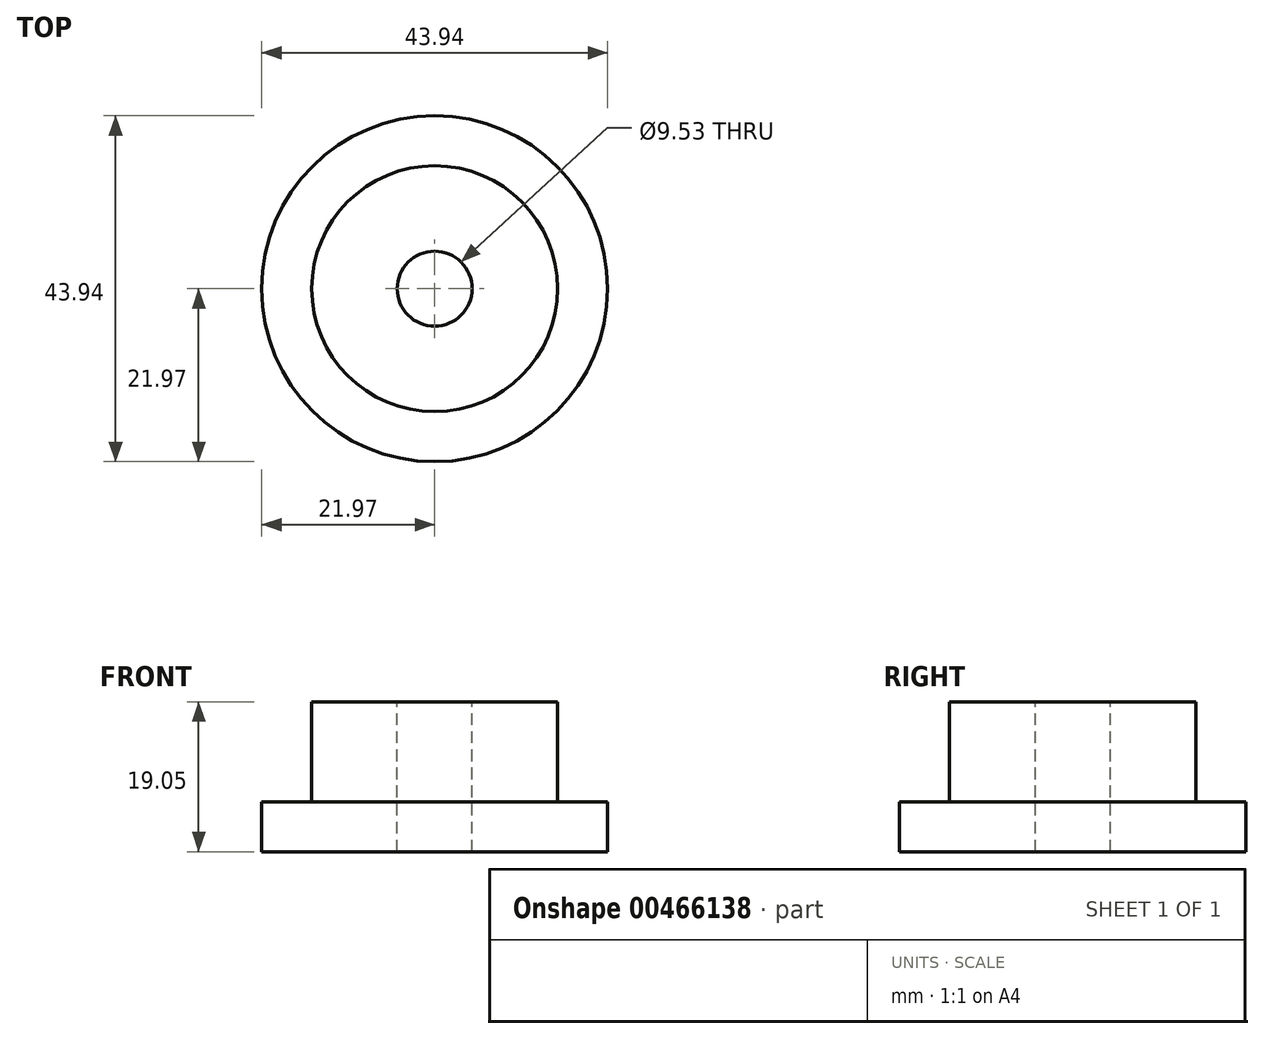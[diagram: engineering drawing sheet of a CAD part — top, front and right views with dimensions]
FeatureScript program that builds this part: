
annotation { "Feature Type Name" : "Feature", "Feature Type Description" : "" }
export const myFeature = defineFeature(function(context is Context, id is Id, definition is map)
    precondition{}
    {
        {
            var Q0;
            Q0=qCreatedBy(makeId("Top.planeOp"),FACE);
            var sketch = newSketch(context, id + "F0", { "sketchPlane" : qUnion([Q0])});
            skCircle(sketch, "E0", {"center": v(0, 0) * mm, "radius": 15.62 * mm});
            skCircle(sketch, "E1.0", {"center": v(0, 0) * mm, "radius": 21.97 * mm});
            skSolve(sketch);
        }
        {
            var Q0;
            Q0 = qSketchRegion(id + "F0", true);
            extrude(context, id + "F1", {"entities" : qUnion([Q0]), "depth" : 6.35 * mm, "offsetDistance" : 25.4 * mm});
        }
        {
            var Q0;
            Q0=makeQuery(id+"F0.imprint","IMPRINT",FACE,{"disambiguationData":[TD([[makeQuery(id+"F0.imprint","IMPRINT",EDGE,{"derivedFrom":sQuery(id+"F0.wireOp",EDGE,"E0")}),1.0]])]});
            extrude(context, id + "F2", {"entities" : qUnion([Q0]), "operationType" : NewBodyOperationType.ADD, "depth" : 19.05 * mm, "offsetDistance" : 25.4 * mm});
        }
        {
            var Q0;
            Q0=makeQuery(id+"F2.opExtrude","CAP_FACE",FACE,{"disambiguationData":[OSD([sQuery(id+"F0.wireOp",EDGE,"E0")])],"isStart":false});
            var sketch = newSketch(context, id + "F3", { "sketchPlane" : qUnion([Q0])});
            skCircle(sketch, "E2", {"center": v(0, 0) * mm, "radius": 4.76 * mm});
            skSolve(sketch);
        }
        {
            var Q0;
            Q0 = qSketchRegion(id + "F3", true);
            extrude(context, id + "F4", {"entities" : qUnion([Q0]), "operationType" : NewBodyOperationType.REMOVE, "endBound" : BoundingType.THROUGH_ALL, "oppositeDirection" : true, "depth" : 25.4 * mm, "offsetDistance" : 25.4 * mm});
        }
    });
